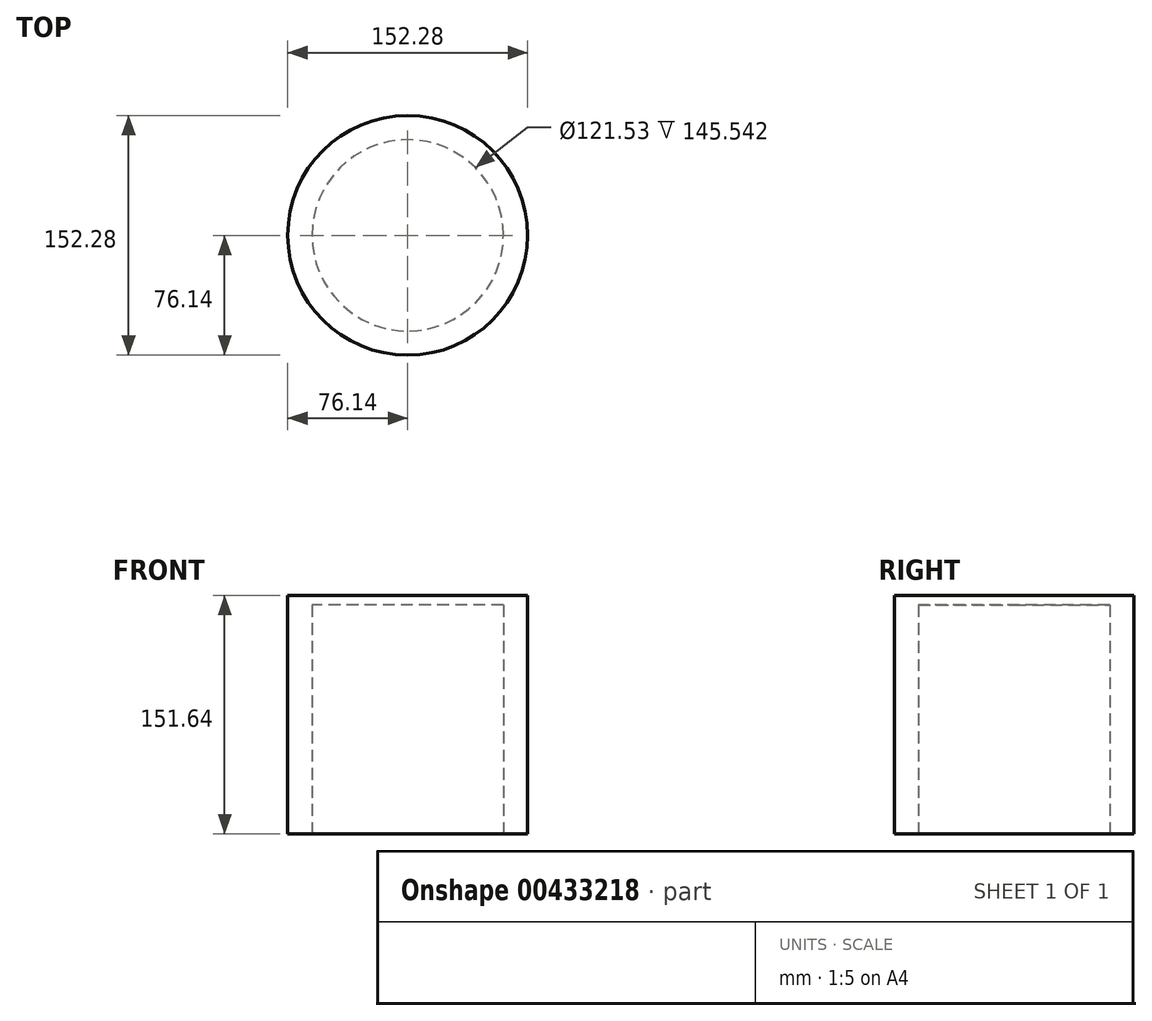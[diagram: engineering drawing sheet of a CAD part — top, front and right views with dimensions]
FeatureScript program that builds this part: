
annotation { "Feature Type Name" : "Feature", "Feature Type Description" : "" }
export const myFeature = defineFeature(function(context is Context, id is Id, definition is map)
    precondition{}
    {
        {
            var Q0;
            Q0=qCreatedBy(makeId("Top.planeOp"),FACE);
            var sketch = newSketch(context, id + "F0", { "sketchPlane" : qUnion([Q0])});
            skCircle(sketch, "E0", {"center": v(0, 0) * mm, "radius": 76.14 * mm});
            skSolve(sketch);
        }
        {
            var Q0;
            Q0=makeQuery(id+"F0.imprint","IMPRINT",FACE,{"disambiguationData":[TD([[makeQuery(id+"F0.imprint","IMPRINT",EDGE,{"derivedFrom":sQuery(id+"F0.wireOp",EDGE,"E0")}),1.0]])]});
            extrude(context, id + "F1", {"entities" : qUnion([Q0]), "depth" : 151.64 * mm});
        }
        {
            var Q0;
            Q0=qCreatedBy(makeId("Top.planeOp"),FACE);
            var sketch = newSketch(context, id + "F2", { "sketchPlane" : qUnion([Q0])});
            skCircle(sketch, "E1", {"center": v(0, 0) * mm, "radius": 67.5 * mm});
            skSolve(sketch);
        }
        {
            var Q0;
            Q0=makeQuery(id+"F2.imprint","IMPRINT",FACE,{"disambiguationData":[TD([[makeQuery(id+"F2.imprint","IMPRINT",EDGE,{"derivedFrom":sQuery(id+"F2.wireOp",EDGE,"E1")}),1.0]])]});
            extrude(context, id + "F3", {"entities" : qUnion([Q0]), "operationType" : NewBodyOperationType.ADD, "depth" : 149.1 * mm});
        }
        {
            var Q0;
            Q0=qCreatedBy(makeId("Top.planeOp"),FACE);
            var sketch = newSketch(context, id + "F4", { "sketchPlane" : qUnion([Q0])});
            skCircle(sketch, "E2", {"center": v(0, 0) * mm, "radius": 68.24 * mm});
            skCircle(sketch, "E3", {"center": v(0, 0) * mm, "radius": 59.9 * mm});
            skCircle(sketch, "E4", {"center": v(0, 0) * mm, "radius": 51.35 * mm});
            skCircle(sketch, "E5", {"center": v(0, 0) * mm, "radius": 42.6 * mm});
            skCircle(sketch, "E6", {"center": v(0, 0) * mm, "radius": 33.25 * mm});
            skSolve(sketch);
        }
        {
            var Q0;
            Q0=makeQuery(id+"F4.imprint","IMPRINT",FACE,{"disambiguationData":[TD([[makeQuery(id+"F4.imprint","IMPRINT",EDGE,{"derivedFrom":sQuery(id+"F4.wireOp",EDGE,"E2")}),1.0]])]});
            extrude(context, id + "F5", {"entities" : qUnion([Q0]), "operationType" : NewBodyOperationType.REMOVE, "oppositeDirection" : true, "depth" : 25.4 * mm});
        }
        {
            var Q0;
            Q0=qCreatedBy(makeId("Top.planeOp"),FACE);
            var sketch = newSketch(context, id + "F6", { "sketchPlane" : qUnion([Q0])});
            skCircle(sketch, "E7", {"center": v(0, 0) * mm, "radius": 60.76 * mm});
            skSolve(sketch);
        }
        {
            var Q0;
            Q0=makeQuery(id+"F6.imprint","IMPRINT",FACE,{"disambiguationData":[TD([[makeQuery(id+"F6.imprint","IMPRINT",EDGE,{"derivedFrom":sQuery(id+"F6.wireOp",EDGE,"E7")}),1.0]])]});
            extrude(context, id + "F7", {"entities" : qUnion([Q0]), "operationType" : NewBodyOperationType.REMOVE, "depth" : 145.54 * mm});
        }
    });
